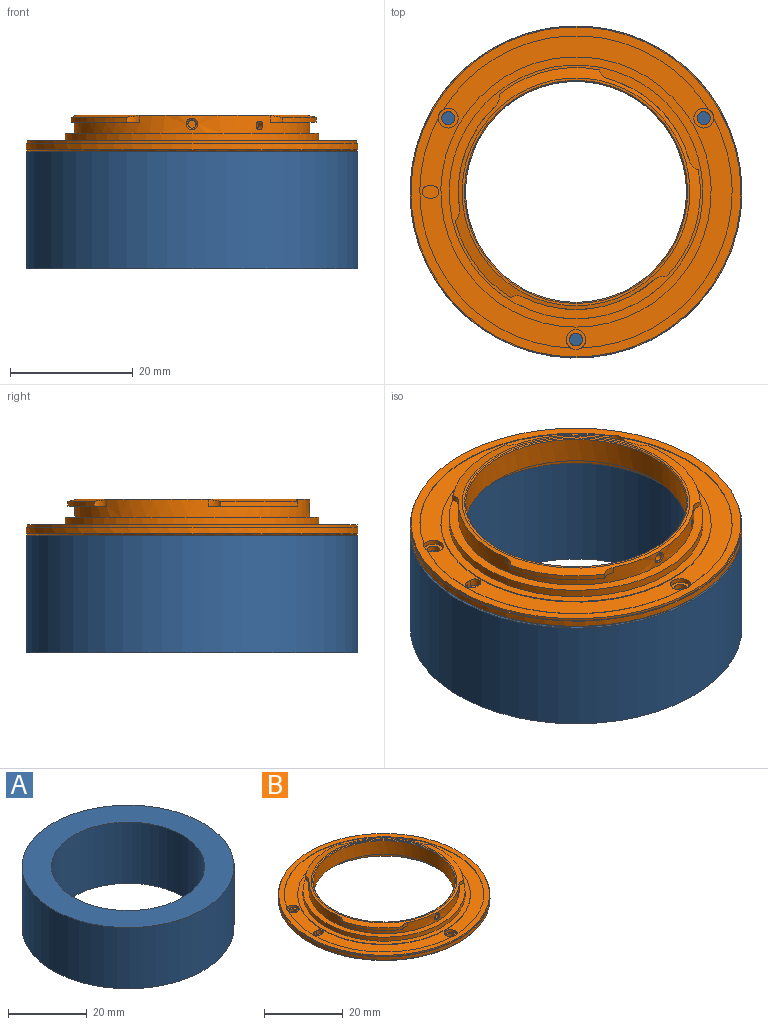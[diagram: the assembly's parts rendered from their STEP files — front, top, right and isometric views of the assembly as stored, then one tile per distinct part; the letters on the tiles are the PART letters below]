
ASSEMBLY  parts=2 mates=1
PART A: 4 faces, bbox 54x54x19.1 mm
  f0: cylinder r=19.48mm len=38.95mm, axis (0,0,-1), area 2331.1mm2, adj f2,f3
  f1: cylinder r=26.99mm len=53.98mm, axis (0,0,-1), area 3230.3mm2, adj f2,f3
  f2: plane 53.98x53.98mm, normal (0,0,1), area 1096.5mm2, adj f0,f1
  f3: plane 53.98x53.98mm, normal (0,0,-1), area 1096.5mm2, adj f0,f1
PART B: 50 faces, bbox 54x54x6 mm
  f0: cylinder r=17.96mm len=35.93mm, axis (0,0,1), area 474.3mm2, adj f23,f45,f46,f47
  f1: cylinder r=25.4mm len=43.14mm, axis (0,0,1), area 6.5mm2, adj f11,f13,f40,f42
  f2: cylinder r=1.05mm len=2.1mm, axis (0,0,1), area 5.9mm2, adj f24,f43
  f3: cylinder r=25.4mm len=37.36mm, axis (0,0,1), area 6.5mm2, adj f11,f13,f38,f40
  f4: cylinder r=1.05mm len=2.1mm, axis (0,0,1), area 5.9mm2, adj f24,f41
  f5: cylinder r=1.05mm len=2.1mm, axis (0,0,1), area 5.9mm2, adj f24,f39
  f6: plane 14.5x11.12mm, normal (0,0,-1), area 17.7mm2, adj f7,f18,f28,f31
  f7: cylinder r=20.21mm len=12.53mm, axis (0,0,1), area 12.8mm2, adj f6,f21,f28,f31
  f8: plane 19.42x7.52mm, normal (0,0,-1), area 20.9mm2, adj f9,f18,f29,f32
  f9: cylinder r=20.21mm len=17.42mm, axis (0,0,1), area 15.2mm2, adj f8,f21,f29,f32
  f10: cylinder r=26.84mm len=53.68mm, axis (0,0,1), area 66.4mm2, adj f11,f26
  f11: plane 53.68x53.68mm, normal (0,0,1), area 235.8mm2, adj f1,f3,f10,f12,f38,f40,f42
  f12: cylinder r=25.4mm len=37.36mm, axis (0,0,1), area 6.5mm2, adj f11,f13,f38,f42
  f13: plane 50.8x50.79mm, normal (0,0,1), area 480.2mm2, adj f1,f3,f12,f14,f33,f34,f35,f36
  f14: cylinder r=21.98mm len=43.97mm, axis (0,0,1), area 17.5mm2, adj f13,f15
  f15: plane 43.97x43.97mm, normal (0,0,1), area 181.1mm2, adj f14,f16
  f16: cylinder r=20.63mm len=41.26mm, axis (0,0,1), area 164.6mm2, adj f15,f17
  f17: plane 41.26x41.26mm, normal (0,0,1), area 187.2mm2, adj f16,f18
  f18: cylinder r=19.13mm len=38.27mm, axis (0,0,1), area 270mm2, adj f6,f8,f17,f19,f21,f27,f28,f29
  f19: plane 18.42x6.32mm, normal (0,0,-1), area 19.2mm2, adj f18,f20,f27,f30
  f20: cylinder r=20.21mm len=16.26mm, axis (0,0,1), area 13.9mm2, adj f19,f21,f27,f30
  f21: cone r=18.52mm half-angle=77.5deg, axis (0,0,-1), area 132.9mm2, adj f7,f9,f18,f20,f22,f27,f28,f29
  f22: plane 37.05x37.05mm, normal (0,0,1), area 43.9mm2, adj f21,f23
  f23: cone r=17.96mm half-angle=45deg, axis (0,0,1), area 28.8mm2, adj f0,f22
  f24: plane 53.21x53.21mm, normal (0,0,-1), area 1022mm2, adj f2,f4,f5,f44,f49
  f25: cylinder r=26.99mm len=53.98mm, axis (0,0,1), area 172.3mm2, adj f26,f49
  f26: plane 53.98x53.98mm, normal (0,0,1), area 24.7mm2, adj f10,f25
  f27: cylinder r=2.22mm len=1.99mm, axis (0,0,1), area 2mm2, adj f18,f19,f20,f21
  f28: cylinder r=2.22mm len=1.97mm, axis (0,0,1), area 2mm2, adj f6,f7,f18,f21
  f29: cylinder r=2.22mm len=1.52mm, axis (0,0,1), area 2mm2, adj f8,f9,f18,f21
  f30: cylinder r=2.22mm len=1.5mm, axis (0,0,1), area 2mm2, adj f18,f19,f20,f21
  f31: cylinder r=2.22mm len=2.1mm, axis (0,0,1), area 2mm2, adj f6,f7,f18,f21
  f32: cylinder r=2.22mm len=2.04mm, axis (0,0,1), area 2mm2, adj f8,f9,f18,f21
  f33: plane 1.27x0.75mm, normal (0,-1,0), area 1mm2, adj f13,f34,f36,f37
  f34: cylinder r=0.99mm len=1.98mm, axis (0,0,1), area 4mm2, adj f13,f33,f35,f37
  f35: plane 1.27x0.75mm, normal (0,1,0), area 1mm2, adj f13,f34,f36,f37
  f36: cylinder r=0.99mm len=1.98mm, axis (0,0,1), area 4mm2, adj f13,f33,f35,f37
  f37: plane 2.73x1.98mm, normal (0,0,1), area 4.6mm2, adj f33,f34,f35,f36
  f38: cylinder r=1.61mm len=3.23mm, axis (0,0,1), area 7.9mm2, adj f3,f11,f12,f13,f39
  f39: plane 3.23x3.23mm, normal (0,0,1), area 4.7mm2, adj f5,f38
  f40: cylinder r=1.61mm len=3.23mm, axis (0,0,1), area 7.9mm2, adj f1,f3,f11,f13,f41
  f41: plane 3.23x3.23mm, normal (0,0,1), area 4.7mm2, adj f4,f40
  f42: cylinder r=1.61mm len=3.23mm, axis (0,0,1), area 7.9mm2, adj f1,f11,f12,f13,f43
  f43: plane 3.23x3.23mm, normal (0,0,1), area 4.7mm2, adj f2,f42
  f44: cylinder r=19.48mm len=38.95mm, axis (0,0,-1), area 194.3mm2, adj f24,f45
  f45: plane 38.95x38.95mm, normal (0,0,-1), area 177.8mm2, adj f0,f44
  f46: cylinder r=0.67mm len=1.77mm, axis (0.57,-0.82,0), area 4.9mm2, adj f0,f18
  f47: cylinder r=0.67mm len=1.33mm, axis (0,-1,0), area 4.2mm2, adj f0,f48
  f48: bspline ~1.87x1.85mm, area 1.5mm2, adj f18,f47
  f49: cone r=26.99mm half-angle=45deg, axis (0,0,1), area 90.7mm2, adj f24,f25
PLACE A t=(-12.36,9.04,-13.21)mm
PLACE B t=(-12.36,9.04,5.84)mm
MATE fastened B.f0 <-> A.f1  axis (0,0,-1) through (-12.36,9.04,5.84)mm
